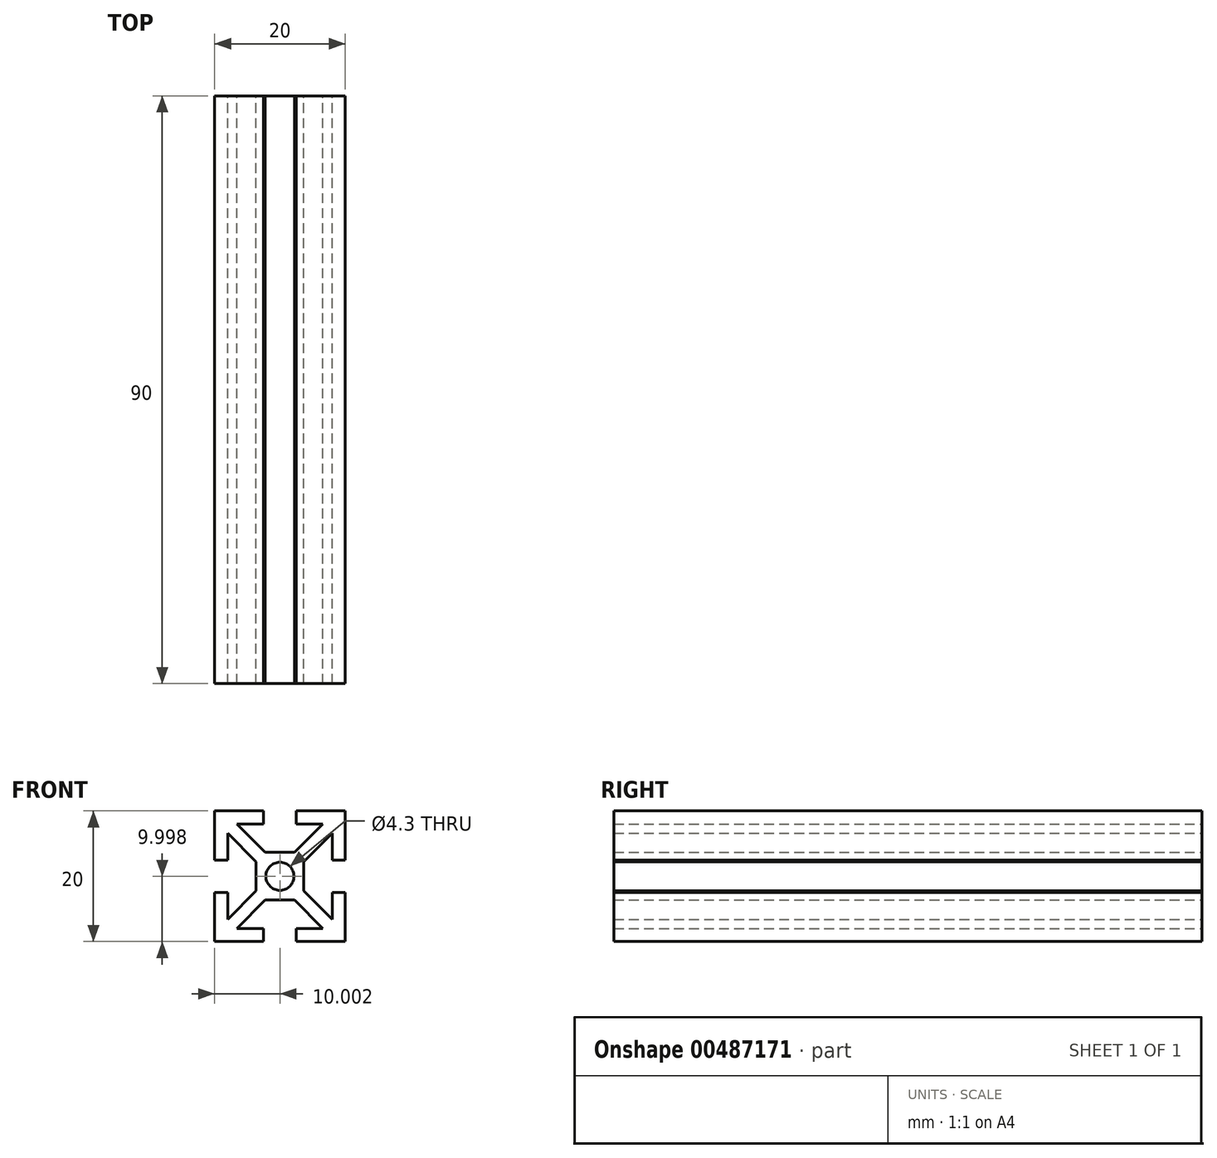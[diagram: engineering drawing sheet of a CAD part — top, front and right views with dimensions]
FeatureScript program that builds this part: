
annotation { "Feature Type Name" : "Feature", "Feature Type Description" : "" }
export const myFeature = defineFeature(function(context is Context, id is Id, definition is map)
    precondition{}
    {
        {
            var Q0;
            Q0=qCreatedBy(makeId("Front.planeOp"),FACE);
            var sketch = newSketch(context, id + "F0", { "sketchPlane" : qUnion([Q0])});
            skLineSegment(sketch, "E0.bottom", {"start": v(-9.74, 9.77) * mm, "end": v(-2.24, 9.77) * mm});
            skLineSegment(sketch, "E0.left", {"start": v(-9.74, 9.77) * mm, "end": v(-9.74, 2.27) * mm});
            skLineSegment(sketch, "E0.right", {"start": v(10.26, 9.77) * mm, "end": v(10.26, 2.27) * mm});
            skArc(sketch, "E1", {"start": v(2.41, -0.23) * mm, "mid": v(0.26, 1.92) * mm, "end": v(-1.89, -0.23) * mm});
            skLineSegment(sketch, "E2.bottom", {"start": v(-1.97, 3.42) * mm, "end": v(2.5, 3.42) * mm});
            skLineSegment(sketch, "E2.left", {"start": v(-3.39, 2) * mm, "end": v(-3.39, -0.23) * mm});
            skLineSegment(sketch, "E2.right", {"start": v(3.91, 2) * mm, "end": v(3.91, -0.23) * mm});
            skLineSegment(sketch, "E3", {"start": v(-2.24, 9.77) * mm, "end": v(-2.24, 7.77) * mm});
            skLineSegment(sketch, "E4", {"start": v(-2.24, 7.77) * mm, "end": v(-6.32, 7.77) * mm});
            skLineSegment(sketch, "E5", {"start": v(2.76, 9.77) * mm, "end": v(2.76, 7.77) * mm});
            skPoint(sketch, "E5.endSnap0", {"position": v(-5.99, 7.77) * mm});
            skLineSegment(sketch, "E6", {"start": v(2.76, 7.77) * mm, "end": v(6.85, 7.77) * mm});
            skLineSegment(sketch, "E7", {"start": v(-7.74, 6.35) * mm, "end": v(-7.74, 2.27) * mm});
            skLineSegment(sketch, "E8", {"start": v(-7.74, 2.27) * mm, "end": v(-9.74, 2.27) * mm});
            skLineSegment(sketch, "E9", {"start": v(-7.74, 6.35) * mm, "end": v(-3.39, 2) * mm});
            skLineSegment(sketch, "E10", {"start": v(-1.97, 3.42) * mm, "end": v(-6.32, 7.77) * mm});
            skPoint(sketch, "E10.endSnap0", {"position": v(-6.32, -0.18) * mm});
            skLineSegment(sketch, "E11", {"start": v(8.26, 6.35) * mm, "end": v(8.26, 2.27) * mm});
            skLineSegment(sketch, "E12", {"start": v(8.26, 2.27) * mm, "end": v(10.26, 2.27) * mm});
            skPoint(sketch, "E13.orphan", {"position": v(10.26, 7.77) * mm});
            skLineSegment(sketch, "E14", {"start": v(2.5, 3.42) * mm, "end": v(6.85, 7.77) * mm});
            skLineSegment(sketch, "E15", {"start": v(3.91, 2) * mm, "end": v(8.26, 6.35) * mm});
            skPoint(sketch, "E16.orphan", {"position": v(-9.74, 7.77) * mm});
            skPoint(sketch, "E17.orphan", {"position": v(-3.39, 3.42) * mm});
            skPoint(sketch, "E18.orphan", {"position": v(3.91, 3.42) * mm});
            skLineSegment(sketch, "E19", {"start": v(-9.74, -0.23) * mm, "end": v(10.26, -0.23) * mm, "construction": true});
            skPoint(sketch, "E0.top.end.orphan", {"position": v(10.26, -10.23) * mm});
            skPoint(sketch, "E0.top.start.orphan", {"position": v(-9.74, -10.23) * mm});
            skLineSegment(sketch, "E20.MirrorCS", {"start": v(-9.74, -10.23) * mm, "end": v(-9.74, -2.73) * mm});
            skLineSegment(sketch, "E21.MirrorCS", {"start": v(-7.74, -2.73) * mm, "end": v(-9.74, -2.73) * mm});
            skLineSegment(sketch, "E22.MirrorCS", {"start": v(-7.74, -6.82) * mm, "end": v(-7.74, -2.73) * mm});
            skLineSegment(sketch, "E23.MirrorCS", {"start": v(-7.74, -6.82) * mm, "end": v(-3.39, -2.47) * mm});
            skLineSegment(sketch, "E24.MirrorCS", {"start": v(-3.39, -2.47) * mm, "end": v(-3.39, -0.23) * mm});
            skArc(sketch, "E25.MirrorCS", {"start": v(2.41, -0.23) * mm, "mid": v(0.26, -2.38) * mm, "end": v(-1.89, -0.23) * mm});
            skLineSegment(sketch, "E26.MirrorCS", {"start": v(-1.97, -3.88) * mm, "end": v(-6.32, -8.23) * mm});
            skLineSegment(sketch, "E27.MirrorCS", {"start": v(-1.97, -3.88) * mm, "end": v(2.5, -3.88) * mm});
            skLineSegment(sketch, "E28.MirrorCS", {"start": v(-2.24, -8.23) * mm, "end": v(-6.32, -8.23) * mm});
            skLineSegment(sketch, "E29.MirrorCS", {"start": v(-2.24, -10.23) * mm, "end": v(-2.24, -8.23) * mm});
            skLineSegment(sketch, "E30.MirrorCS", {"start": v(-9.74, -10.23) * mm, "end": v(-2.24, -10.23) * mm});
            skLineSegment(sketch, "E31.MirrorCS", {"start": v(2.76, -10.23) * mm, "end": v(2.76, -8.23) * mm});
            skLineSegment(sketch, "E32.MirrorCS", {"start": v(2.76, -8.23) * mm, "end": v(6.85, -8.23) * mm});
            skLineSegment(sketch, "E33.MirrorCS", {"start": v(2.5, -3.88) * mm, "end": v(6.85, -8.23) * mm});
            skLineSegment(sketch, "E34.MirrorCS", {"start": v(3.91, -2.47) * mm, "end": v(8.26, -6.82) * mm});
            skLineSegment(sketch, "E35.MirrorCS", {"start": v(8.26, -6.82) * mm, "end": v(8.26, -2.73) * mm});
            skLineSegment(sketch, "E36.MirrorCS", {"start": v(8.26, -2.73) * mm, "end": v(10.26, -2.73) * mm});
            skLineSegment(sketch, "E37.MirrorCS", {"start": v(10.26, -10.23) * mm, "end": v(10.26, -2.73) * mm});
            skLineSegment(sketch, "E38.MirrorCS", {"start": v(3.91, -2.47) * mm, "end": v(3.91, -0.23) * mm});
            skLineSegment(sketch, "E39.trimOffspring", {"start": v(2.76, 9.77) * mm, "end": v(10.26, 9.77) * mm});
            skLineSegment(sketch, "E40.trimOffspring", {"start": v(2.76, -10.23) * mm, "end": v(10.26, -10.23) * mm});
            skSolve(sketch);
        }
        {
            var Q0;
            Q0=makeQuery(id+"F0.imprint","IMPRINT",FACE,{"disambiguationData":[TD([[makeQuery(id+"F0.imprint","IMPRINT",EDGE,{"derivedFrom":sQuery(id+"F0.wireOp",EDGE,"E0.bottom")}),-1.0]])]});
            extrude(context, id + "F1", {"entities" : qUnion([Q0]), "depth" : 90 * mm});
        }
    });
